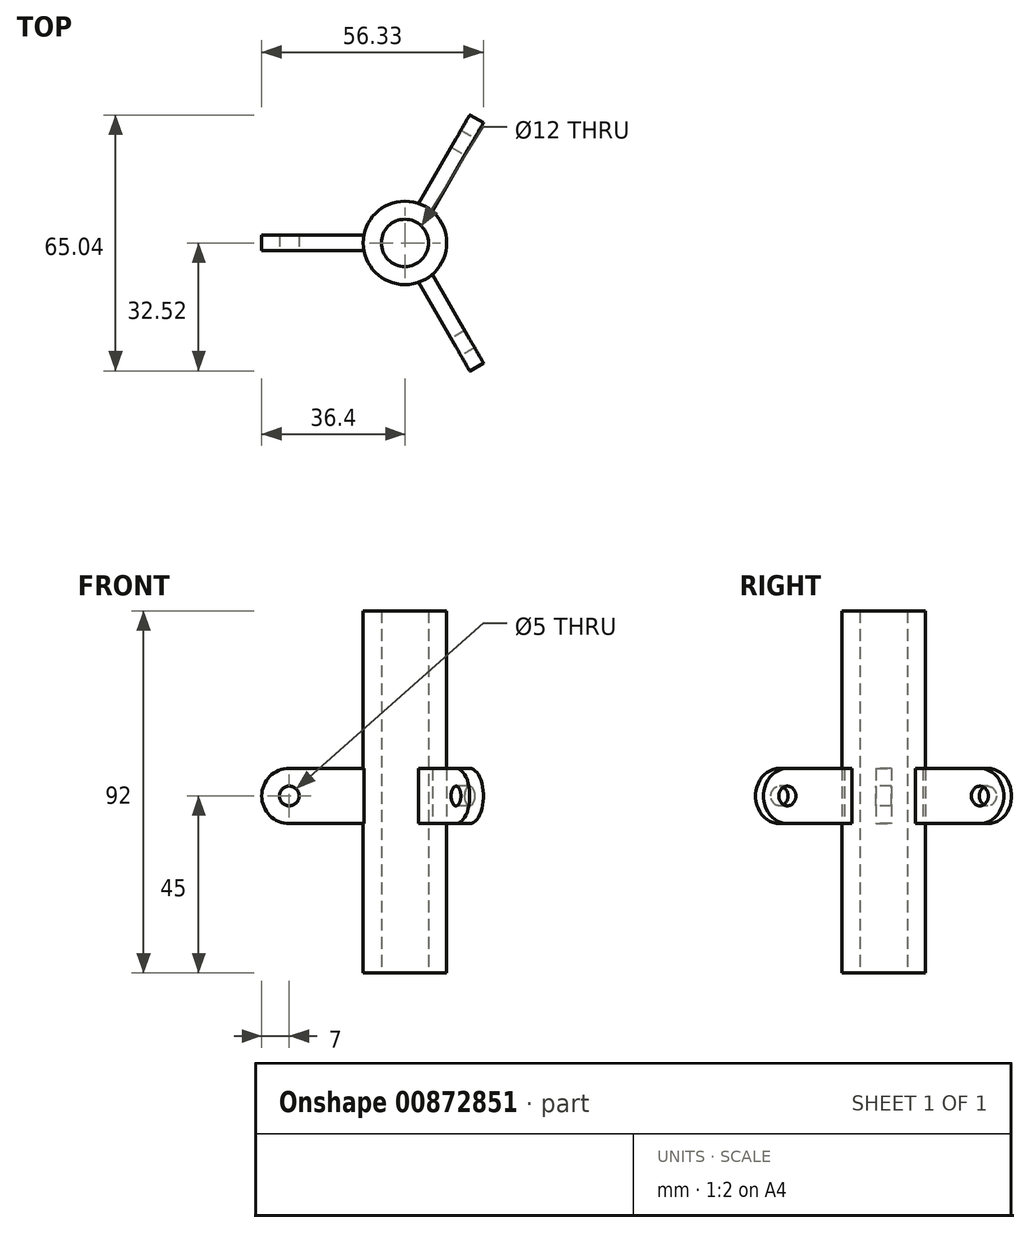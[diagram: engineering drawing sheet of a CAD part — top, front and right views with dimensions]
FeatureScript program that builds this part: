
annotation { "Feature Type Name" : "Feature", "Feature Type Description" : "" }
export const myFeature = defineFeature(function(context is Context, id is Id, definition is map)
    precondition{}
    {
        {
            var Q0;
            Q0=qCreatedBy(makeId("Top.planeOp"),FACE);
            var sketch = newSketch(context, id + "F0", { "sketchPlane" : qUnion([Q0])});
            skCircle(sketch, "E0", {"center": v(0, 0) * mm, "radius": 10.6 * mm});
            skSolve(sketch);
        }
        {
            var Q0;
            Q0 = qSketchRegion(id + "F0", true);
            extrude(context, id + "F1", {"entities" : qUnion([Q0]), "depth" : (460 / 5) * mm, "offsetDistance" : 25 * mm});
        }
        {
            var Q0;
            Q0=makeQuery(id+"F1.opExtrude","CAP_FACE",FACE,{"disambiguationData":[OSD([sQuery(id+"F0.wireOp",EDGE,"E0")])],"isStart":true});
            var sketch = newSketch(context, id + "F2", { "sketchPlane" : qUnion([Q0])});
            skCircle(sketch, "E1", {"center": v(0, 0) * mm, "radius": 6 * mm});
            skSolve(sketch);
        }
        {
            var Q0;
            Q0 = qSketchRegion(id + "F2", true);
            extrude(context, id + "F3", {"entities" : qUnion([Q0]), "operationType" : NewBodyOperationType.REMOVE, "oppositeDirection" : true, "depth" : 98.1 * mm, "offsetDistance" : 25 * mm});
        }
        {
            var Q0;
            Q0=qCreatedBy(makeId("Front.planeOp"),FACE);
            var sketch = newSketch(context, id + "F4", { "sketchPlane" : qUnion([Q0])});
            skArc(sketch, "E2", {"start": v(-29.4, 52) * mm, "mid": v(-36.4, 45) * mm, "end": v(-29.4, 38) * mm});
            skLineSegment(sketch, "E3", {"start": v(-29.4, 52) * mm, "end": v(-9.78, 52) * mm});
            skLineSegment(sketch, "E4", {"start": v(-29.4, 38) * mm, "end": v(-9.78, 38) * mm});
            skLineSegment(sketch, "E5", {"start": v(-9.78, 52) * mm, "end": v(-9.78, 38) * mm});
            skSolve(sketch);
        }
        {
            var Q0;
            Q0 = qSketchRegion(id + "F4", true);
            extrude(context, id + "F5", {"entities" : qUnion([Q0]), "operationType" : NewBodyOperationType.ADD, "endBound" : BoundingType.SYMMETRIC, "depth" : 4 * mm, "offsetDistance" : 25 * mm});
        }
        {
            var Q0;
            Q0=makeQuery(id+"F1.opExtrude","SWEPT_BODY",BODY,{"disambiguationData":[OSD([sQuery(id+"F0.wireOp",EDGE,"E0")])]});
            var Q1;
            Q1=makeQuery(id+"F1.opExtrude","SWEPT_FACE",FACE,{"disambiguationData":[OSD([sQuery(id+"F0.wireOp",EDGE,"E0")])]});
            circularPattern(context, id + "F6", {"operationType" : NewBodyOperationType.ADD, "entities" : qUnion([Q0]), "axis" : qUnion([Q1]), "angle" : 360 * degree, "instanceCount" : 3, "equalSpace" : true});
        }
        {
            var Q0;
            Q0=makeQuery(id+"F5.opExtrude","CAP_FACE",FACE,{"disambiguationData":[OSD([sQuery(id+"F4.wireOp",EDGE,"E2"),sQuery(id+"F4.wireOp",EDGE,"E3"),sQuery(id+"F4.wireOp",EDGE,"E4"),sQuery(id+"F4.wireOp",EDGE,"E5")])],"isStart":false});
            var sketch = newSketch(context, id + "F7", { "sketchPlane" : qUnion([Q0])});
            skCircle(sketch, "E6", {"center": v(-29.4, 45) * mm, "radius": 2.5 * mm});
            skSolve(sketch);
        }
        {
            var Q0;
            Q0 = qSketchRegion(id + "F7", true);
            extrude(context, id + "F8", {"entities" : qUnion([Q0]), "operationType" : NewBodyOperationType.REMOVE, "endBound" : BoundingType.UP_TO_NEXT, "oppositeDirection" : true, "depth" : 25 * mm, "offsetDistance" : 25 * mm});
        }
        {
            var Q0;
            Q0=makeQuery(id+"F6.opPattern","COPY",FACE,{"derivedFrom":makeQuery(id+"F5.opExtrude","CAP_FACE",FACE,{"disambiguationData":[OSD([sQuery(id+"F4.wireOp",EDGE,"E2"),sQuery(id+"F4.wireOp",EDGE,"E3"),sQuery(id+"F4.wireOp",EDGE,"E4"),sQuery(id+"F4.wireOp",EDGE,"E5")])],"isStart":true}),"instanceName":"2"});
            var sketch = newSketch(context, id + "F9", { "sketchPlane" : qUnion([Q0])});
            skCircle(sketch, "E7", {"center": v(29.4, 45) * mm, "radius": 2.5 * mm});
            skSolve(sketch);
        }
        {
            var Q0;
            Q0 = qSketchRegion(id + "F9", true);
            extrude(context, id + "F10", {"entities" : qUnion([Q0]), "operationType" : NewBodyOperationType.REMOVE, "endBound" : BoundingType.UP_TO_NEXT, "oppositeDirection" : true, "depth" : 25 * mm, "offsetDistance" : 25 * mm});
        }
        {
            var Q0;
            Q0=makeQuery(id+"F6.opPattern","COPY",FACE,{"derivedFrom":makeQuery(id+"F5.opExtrude","CAP_FACE",FACE,{"disambiguationData":[OSD([sQuery(id+"F4.wireOp",EDGE,"E2"),sQuery(id+"F4.wireOp",EDGE,"E3"),sQuery(id+"F4.wireOp",EDGE,"E4"),sQuery(id+"F4.wireOp",EDGE,"E5")])],"isStart":true}),"instanceName":"1"});
            var sketch = newSketch(context, id + "F11", { "sketchPlane" : qUnion([Q0])});
            skCircle(sketch, "E8", {"center": v(29.4, 45) * mm, "radius": 2.5 * mm});
            skSolve(sketch);
        }
        {
            var Q0;
            Q0 = qSketchRegion(id + "F11", true);
            extrude(context, id + "F12", {"entities" : qUnion([Q0]), "operationType" : NewBodyOperationType.REMOVE, "endBound" : BoundingType.UP_TO_NEXT, "oppositeDirection" : true, "depth" : 25 * mm, "offsetDistance" : 25 * mm});
        }
    });
